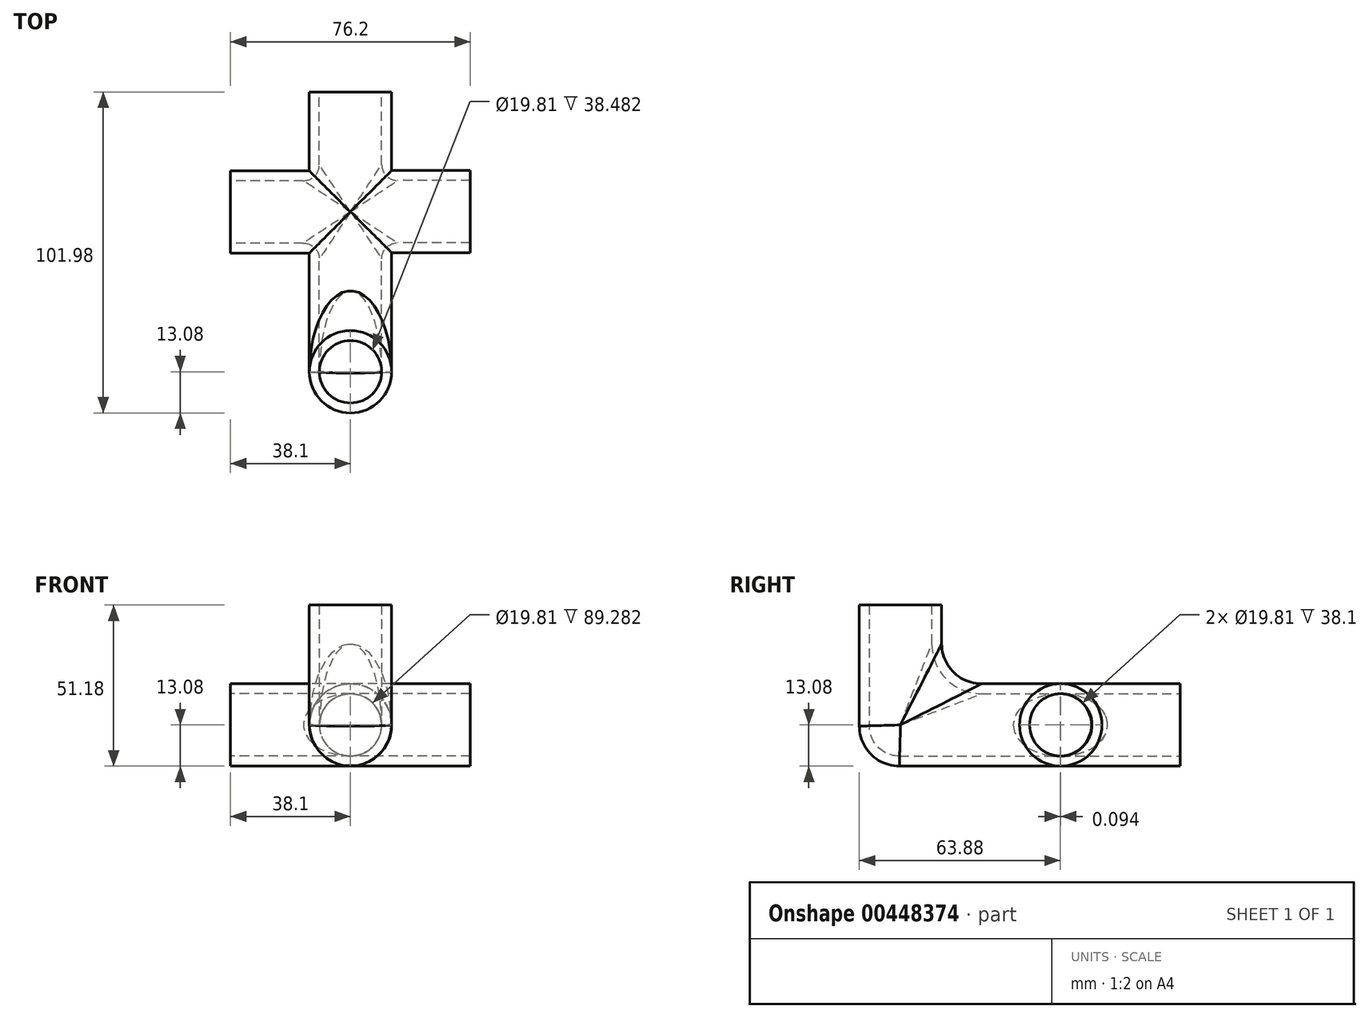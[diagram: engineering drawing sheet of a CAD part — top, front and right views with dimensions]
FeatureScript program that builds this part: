
annotation { "Feature Type Name" : "Feature", "Feature Type Description" : "" }
export const myFeature = defineFeature(function(context is Context, id is Id, definition is map)
    precondition{}
    {
        {
            var Q0;
            Q0=qCreatedBy(makeId("Right.planeOp"),FACE);
            var sketch = newSketch(context, id + "F0", { "sketchPlane" : qUnion([Q0])});
            skLineSegment(sketch, "E0", {"start": v(0, 38.1) * mm, "end": v(0, 0) * mm});
            skLineSegment(sketch, "E1", {"start": v(0, 0) * mm, "end": v(25.4, 0) * mm});
            skPoint(sketch, "E2.visualSharp", {"position": v(0, 0) * mm});
            skSolve(sketch);
        }
        {
            var Q0;
            Q0=qCreatedBy(makeId("Top.planeOp"),FACE);
            cPlane(context, id + "F1", {"entities" : qUnion([Q0]), "cplaneType" : CPlaneType.OFFSET, "offset" : 38.1 * mm, "width" : 152.4 * mm, "height" : 152.4 * mm});
        }
        {
            var Q0;
            Q0=qCreatedBy(id+"F1.planeOp",FACE);
            var sketch = newSketch(context, id + "F2", { "sketchPlane" : qUnion([Q0])});
            skCircle(sketch, "E3", {"center": v(0, 0) * mm, "radius": 13.08 * mm});
            skSolve(sketch);
        }
        {
            var Q0;
            Q0=makeQuery(id+"F2.imprint","IMPRINT",FACE,{"disambiguationData":[TD([[makeQuery(id+"F2.imprint","IMPRINT",EDGE,{"derivedFrom":sQuery(id+"F2.wireOp",EDGE,"E3")}),1.0]])]});
            var Q1;
            Q1=sQuery(id+"F0.wireOp",EDGE,"E0");
            var Q2;
            Q2=sQuery(id+"F0.wireOp",EDGE,"E1");
            sweep(context, id + "F3", {"profiles" : qUnion([Q0]), "path" : qUnion([Q1, Q2])});
        }
        {
            var Q0;
            Q0=qCreatedBy(makeId("Top.planeOp"),FACE);
            var sketch = newSketch(context, id + "F4", { "sketchPlane" : qUnion([Q0])});
            skLineSegment(sketch, "E4", {"start": v(0, 50.8) * mm, "end": v(-38.1, 50.8) * mm});
            skLineSegment(sketch, "E5.0", {"start": v(-13.08, 25.4) * mm, "end": v(13.08, 25.4) * mm, "construction": true});
            skLineSegment(sketch, "E6", {"start": v(0, 50.8) * mm, "end": v(0, 25.4) * mm});
            skSolve(sketch);
        }
        {
            var Q0;
            Q0=makeQuery(id+"F3.opSweep","CAP_FACE",FACE,{"disambiguationData":[OSD([sQuery(id+"F0.wireOp",VERTEX,"E1.end"),sQuery(id+"F2.wireOp",EDGE,"E3")])],"isStart":false});
            var Q1;
            Q1=sQuery(id+"F4.wireOp",EDGE,"E6");
            var Q2;
            Q2=sQuery(id+"F4.wireOp",EDGE,"E4");
            sweep(context, id + "F5", {"operationType" : NewBodyOperationType.ADD, "profiles" : qUnion([Q0]), "path" : qUnion([Q1, Q2])});
        }
        {
            var Q0;
            Q0=qCreatedBy(makeId("Right.planeOp"),FACE);
            var sketch = newSketch(context, id + "F6", { "sketchPlane" : qUnion([Q0])});
            skCircle(sketch, "E7.0", {"center": v(50.8, 0) * mm, "radius": 13.08 * mm, "construction": true});
            skLineSegment(sketch, "E8", {"start": v(50.8, 0) * mm, "end": v(88.9, 0) * mm});
            skSolve(sketch);
        }
        {
            var Q0;
            Q0=qCreatedBy(makeId("Front.planeOp"),FACE);
            var Q1;
            Q1=sQuery(id+"F6.wireOp",VERTEX,"E8.end");
            cPlane(context, id + "F7", {"entities" : qUnion([Q0, Q1]), "cplaneType" : CPlaneType.PLANE_POINT, "offset" : 25.4 * mm, "oppositeDirection" : true, "width" : 152.4 * mm, "height" : 152.4 * mm});
        }
        {
            var Q0;
            Q0=qCreatedBy(id+"F7.planeOp",FACE);
            var sketch = newSketch(context, id + "F8", { "sketchPlane" : qUnion([Q0])});
            skCircle(sketch, "E9", {"center": v(0, 0) * mm, "radius": 13.08 * mm});
            skSolve(sketch);
        }
        {
            var Q0;
            Q0=makeQuery(id+"F8.imprint","IMPRINT",FACE,{"disambiguationData":[TD([[makeQuery(id+"F8.imprint","IMPRINT",EDGE,{"derivedFrom":sQuery(id+"F8.wireOp",EDGE,"E9")}),1.0]])]});
            var Q1;
            Q1=sQuery(id+"F6.wireOp",EDGE,"E8");
            sweep(context, id + "F9", {"operationType" : NewBodyOperationType.ADD, "profiles" : qUnion([Q0]), "path" : qUnion([Q1])});
        }
        {
            var Q0;
            Q0=qCreatedBy(makeId("Top.planeOp"),FACE);
            var sketch = newSketch(context, id + "F10", { "sketchPlane" : qUnion([Q0])});
            skLineSegment(sketch, "E10.0", {"start": v(0, 50.8) * mm, "end": v(-38.1, 50.8) * mm, "construction": true});
            skLineSegment(sketch, "E11", {"start": v(0, 50.8) * mm, "end": v(38.1, 50.8) * mm});
            skSolve(sketch);
        }
        {
            var Q0;
            Q0=qCreatedBy(makeId("Right.planeOp"),FACE);
            var Q1;
            Q1=sQuery(id+"F10.wireOp",VERTEX,"E11.end");
            cPlane(context, id + "F11", {"entities" : qUnion([Q0, Q1]), "cplaneType" : CPlaneType.PLANE_POINT, "offset" : 25.4 * mm, "width" : 152.4 * mm, "height" : 152.4 * mm});
        }
        {
            var Q0;
            Q0=qCreatedBy(id+"F11.planeOp",FACE);
            var sketch = newSketch(context, id + "F12", { "sketchPlane" : qUnion([Q0])});
            skCircle(sketch, "E12", {"center": v(50.9, 0) * mm, "radius": 13.08 * mm});
            skSolve(sketch);
        }
        {
            var Q0;
            Q0=makeQuery(id+"F12.imprint","IMPRINT",FACE,{"disambiguationData":[TD([[makeQuery(id+"F12.imprint","IMPRINT",EDGE,{"derivedFrom":sQuery(id+"F12.wireOp",EDGE,"E12")}),1.0]])]});
            var Q1;
            Q1=sQuery(id+"F10.wireOp",EDGE,"E11");
            sweep(context, id + "F13", {"operationType" : NewBodyOperationType.ADD, "profiles" : qUnion([Q0]), "path" : qUnion([Q1])});
        }
        {
            var Q0;
            Q0=makeQuery(id+"F3.opSweep","MID_CAP_EDGE",EDGE,{"disambiguationData":[OSD([sQuery(id+"F0.wireOp",VERTEX,"E1.start"),sQuery(id+"F2.wireOp",EDGE,"E3")])],"capPos":1.0});
            fillet(context, id + "F14", {"entities" : qUnion([Q0]), "radius" : 12.7 * mm, "tangentPropagation" : true, "allowEdgeOverflow" : false});
        }
        {
            var Q0;
            Q0=makeQuery(id+"F5.opSweep","CAP_FACE",FACE,{"disambiguationData":[OSD([sQuery(id+"F0.wireOp",VERTEX,"E1.end"),sQuery(id+"F2.wireOp",EDGE,"E3"),sQuery(id+"F4.wireOp",VERTEX,"E4.end")])],"isStart":false});
            var Q1;
            Q1=makeQuery(id+"F9.opSweep","CAP_FACE",FACE,{"disambiguationData":[OSD([sQuery(id+"F6.wireOp",VERTEX,"E8.end"),sQuery(id+"F8.wireOp",EDGE,"E9")])],"isStart":true});
            var Q2;
            Q2=makeQuery(id+"F13.opSweep","CAP_FACE",FACE,{"disambiguationData":[OSD([sQuery(id+"F10.wireOp",VERTEX,"E11.end"),sQuery(id+"F12.wireOp",EDGE,"E12")])],"isStart":true});
            var Q3;
            Q3=makeQuery(id+"F3.opSweep","CAP_FACE",FACE,{"disambiguationData":[OSD([sQuery(id+"F0.wireOp",VERTEX,"E0.start"),sQuery(id+"F2.wireOp",EDGE,"E3")])],"isStart":true});
            shell(context, id + "F15", {"entities" : qUnion([Q0, Q1, Q2, Q3]), "thickness" : 3.17 * mm});
        }
        {
            var Q0;
            {var subQ0=sQuery(id+"F12.wireOp",EDGE,"E12");var subQ1=sQuery(id+"F10.wireOp",EDGE,"E11");var subQ2=sQuery(id+"F8.wireOp",EDGE,"E9");var subQ3=sQuery(id+"F6.wireOp",EDGE,"E8");var subQ4=sQuery(id+"F4.wireOp",EDGE,"E6");var subQ5=sQuery(id+"F2.wireOp",EDGE,"E3");var subQ6=sQuery(id+"F0.wireOp",VERTEX,"E1.end");var subQ7=sQuery(id+"F0.wireOp",EDGE,"E1");Q0=makeQuery(id+"F15.opShell","OFFSET_EDGE",EDGE,{"disambiguationData":[OSD([subQ6,subQ7,subQ5,subQ4,subQ3,subQ2,subQ1,subQ0]),TDD([makeQuery(id+"F13.boolean.opBoolean","INTERSECT",EDGE,{"disambiguationData":[OD(0.0)],"derivedFrom":[makeQuery(id+"F9.boolean.opBoolean","MERGE",FACE,{"derivedFrom":[makeQuery(id+"F5.boolean.opBoolean","MERGE",FACE,{"derivedFrom":[makeQuery(id+"F3.opSweep","SWEPT_FACE",FACE,{"disambiguationData":[OSD([subQ7,subQ5])]}),makeQuery(id+"F5.opSweep","SWEPT_FACE",FACE,{"disambiguationData":[OSD([subQ6,subQ5,subQ4])]})]}),makeQuery(id+"F9.opSweep","SWEPT_FACE",FACE,{"disambiguationData":[OSD([subQ3,subQ2])]})]}),makeQuery(id+"F13.opSweep","SWEPT_FACE",FACE,{"disambiguationData":[OSD([subQ1,subQ0])]})]})])]});}
            var Q1;
            {var subQ0=sQuery(id+"F12.wireOp",EDGE,"E12");var subQ1=sQuery(id+"F10.wireOp",EDGE,"E11");var subQ2=sQuery(id+"F8.wireOp",EDGE,"E9");var subQ3=sQuery(id+"F6.wireOp",EDGE,"E8");var subQ4=sQuery(id+"F4.wireOp",EDGE,"E6");var subQ5=sQuery(id+"F2.wireOp",EDGE,"E3");var subQ6=sQuery(id+"F0.wireOp",VERTEX,"E1.end");var subQ7=sQuery(id+"F0.wireOp",EDGE,"E1");Q1=makeQuery(id+"F15.opShell","OFFSET_EDGE",EDGE,{"disambiguationData":[OSD([subQ6,subQ7,subQ5,subQ4,subQ3,subQ2,subQ1,subQ0]),TDD([makeQuery(id+"F13.boolean.opBoolean","INTERSECT",EDGE,{"disambiguationData":[OD(1.0)],"derivedFrom":[makeQuery(id+"F9.boolean.opBoolean","MERGE",FACE,{"derivedFrom":[makeQuery(id+"F5.boolean.opBoolean","MERGE",FACE,{"derivedFrom":[makeQuery(id+"F3.opSweep","SWEPT_FACE",FACE,{"disambiguationData":[OSD([subQ7,subQ5])]}),makeQuery(id+"F5.opSweep","SWEPT_FACE",FACE,{"disambiguationData":[OSD([subQ6,subQ5,subQ4])]})]}),makeQuery(id+"F9.opSweep","SWEPT_FACE",FACE,{"disambiguationData":[OSD([subQ3,subQ2])]})]}),makeQuery(id+"F13.opSweep","SWEPT_FACE",FACE,{"disambiguationData":[OSD([subQ1,subQ0])]})]})])]});}
            var Q2;
            Q2=makeQuery(id+"F15.opShell","OFFSET_EDGE",EDGE,{"disambiguationData":[OSD([sQuery(id+"F0.wireOp",VERTEX,"E1.end"),sQuery(id+"F2.wireOp",EDGE,"E3"),sQuery(id+"F4.wireOp",EDGE,"E4"),sQuery(id+"F6.wireOp",EDGE,"E8"),sQuery(id+"F8.wireOp",EDGE,"E9")])]});
            var Q3;
            Q3=makeQuery(id+"F15.opShell","OFFSET_EDGE",EDGE,{"disambiguationData":[OSD([sQuery(id+"F0.wireOp",VERTEX,"E1.end"),sQuery(id+"F2.wireOp",EDGE,"E3"),sQuery(id+"F4.wireOp",VERTEX,"E4.start")])]});
            var Q4;
            {var subQ0=sQuery(id+"F2.wireOp",EDGE,"E3");var subQ1=sQuery(id+"F0.wireOp",EDGE,"E0");var subQ2=sQuery(id+"F0.wireOp",VERTEX,"E1.start");Q4=makeQuery(id+"F15.opShell","OFFSET_EDGE",EDGE,{"disambiguationData":[OSD([subQ2,subQ1,subQ0]),TDD([makeQuery(id+"F14.opFillet","BLEND_EDGE",EDGE,{"disambiguationData":[OD(1.0)],"blendedFrom":[makeQuery(id+"F3.opSweep","MID_CAP_EDGE",EDGE,{"disambiguationData":[OSD([subQ2,subQ0])],"capPos":1.0}),makeQuery(id+"F3.opSweep","SWEPT_FACE",FACE,{"disambiguationData":[OSD([subQ1,subQ0])]})],"blendedInto":[makeQuery(id+"F3.opSweep","SWEPT_FACE",FACE,{"disambiguationData":[OSD([subQ1,subQ0])]})]})])]});}
            fillet(context, id + "F16", {"entities" : qUnion([Q0, Q1, Q2, Q3, Q4]), "radius" : 5.08 * mm, "tangentPropagation" : true, "allowEdgeOverflow" : false});
        }
    });
